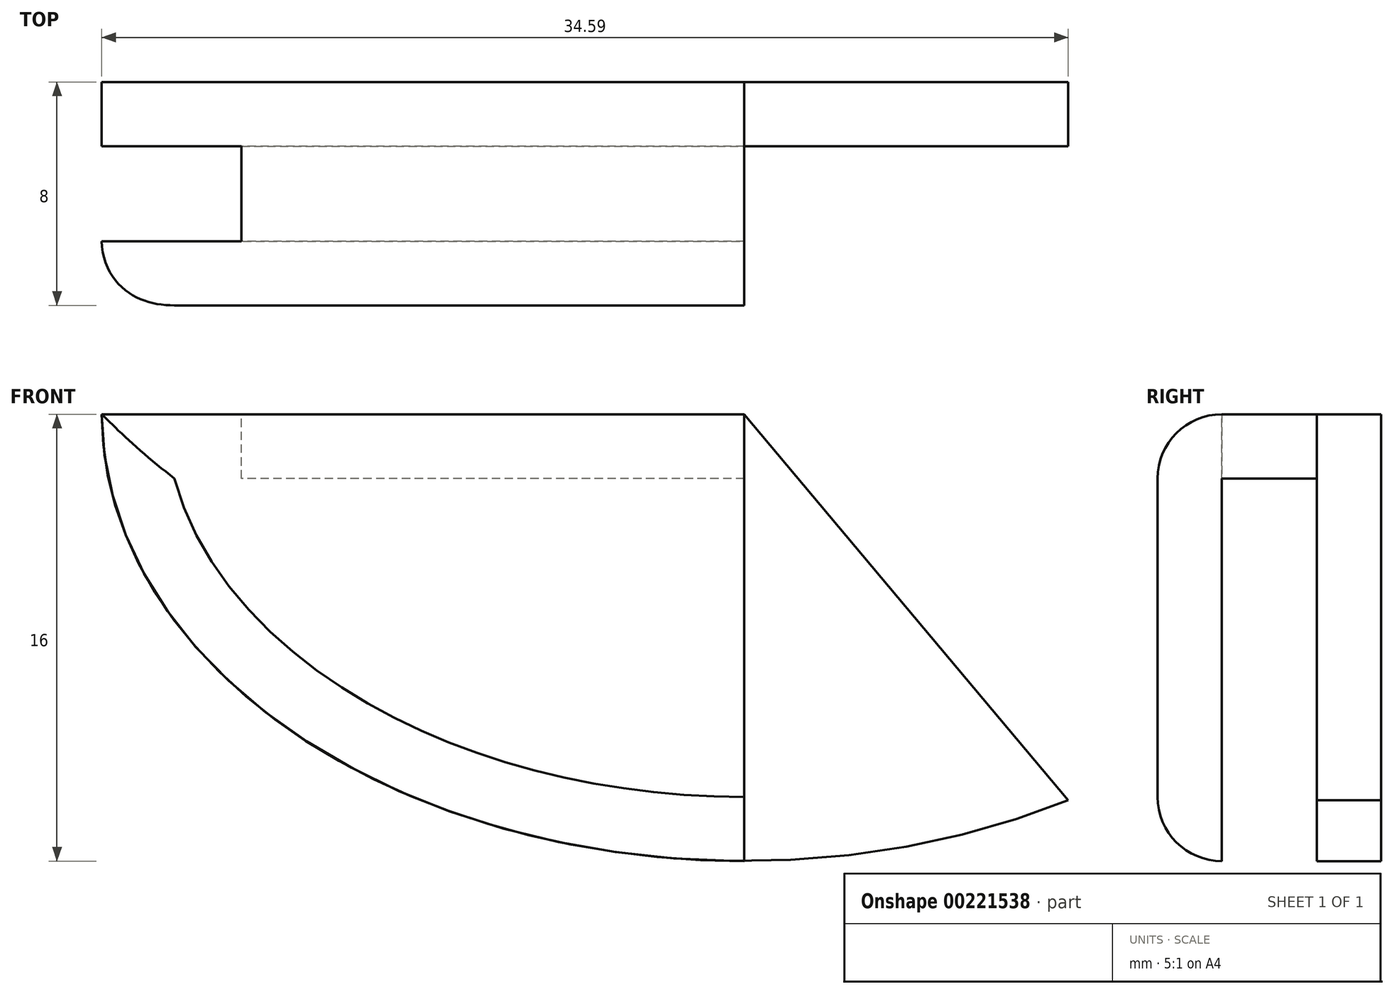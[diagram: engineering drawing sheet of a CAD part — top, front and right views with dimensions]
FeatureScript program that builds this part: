
annotation { "Feature Type Name" : "Feature", "Feature Type Description" : "" }
export const myFeature = defineFeature(function(context is Context, id is Id, definition is map)
    precondition{}
    {
        {
            var Q0;
            Q0=qCreatedBy(makeId("Front.planeOp"),FACE);
            var sketch = newSketch(context, id + "F0", { "sketchPlane" : qUnion([Q0])});
            skEllipse(sketch, "E0", {"center": v(0, 0) * mm, "majorRadius": 23 * mm, "minorRadius": 16 * mm, "majorAxis": v(-1, 0)});
            skLineSegment(sketch, "E1", {"start": v(-23, 0) * mm, "end": v(0, 0) * mm});
            skLineSegment(sketch, "E2", {"start": v(0, -16) * mm, "end": v(0, 0) * mm});
            skLineSegment(sketch, "E3", {"start": v(0, -2.3) * mm, "end": v(-22.76, -2.3) * mm});
            skLineSegment(sketch, "E4", {"start": v(0, 0) * mm, "end": v(11.6, -13.82) * mm});
            skLineSegment(sketch, "E5", {"start": v(-18, -2.3) * mm, "end": v(-18, 0) * mm});
            skSolve(sketch);
        }
        {
            var Q0;
            {var subQ5=sQuery(id+"F0.wireOp",EDGE,"E5");Q0=makeQuery(id+"F0.imprint","IMPRINT",FACE,{"disambiguationData":[TD([[makeQuery(id+"F0.imprint","IMPRINT",EDGE,{"derivedFrom":subQ5}),1.0]])]});}
            var Q1;
            {var subQ3=sQuery(id+"F0.wireOp",EDGE,"E5");Q1=makeQuery(id+"F0.imprint","IMPRINT",FACE,{"disambiguationData":[TD([[makeQuery(id+"F0.imprint","IMPRINT",EDGE,{"derivedFrom":subQ3}),-1.0]])]});}
            var Q2;
            {var subQ0=sQuery(id+"F0.wireOp",EDGE,"E2");var subQ1=sQuery(id+"F0.wireOp",EDGE,"E0");var subQ2=makeQuery(id+"F0.imprint","INTERSECT",VERTEX,{"derivedFrom":[subQ1,subQ0]});Q2=makeQuery(id+"F0.imprint","IMPRINT",FACE,{"disambiguationData":[TD([[makeQuery(id+"F0.imprint","IMPRINT",EDGE,{"disambiguationData":[TD([[subQ2,1.0]])],"derivedFrom":subQ1}),1.0]])]});}
            var Q3;
            {var subQ3=sQuery(id+"F0.wireOp",EDGE,"E4");Q3=makeQuery(id+"F0.imprint","IMPRINT",FACE,{"disambiguationData":[TD([[makeQuery(id+"F0.imprint","IMPRINT",EDGE,{"derivedFrom":subQ3}),-1.0]])]});}
            extrude(context, id + "F1", {"entities" : qUnion([Q0, Q1, Q2, Q3]), "oppositeDirection" : true, "depth" : 4 * mm});
        }
        {
            var Q0;
            {var subQ3=sQuery(id+"F0.wireOp",EDGE,"E5");Q0=makeQuery(id+"F0.imprint","IMPRINT",FACE,{"disambiguationData":[TD([[makeQuery(id+"F0.imprint","IMPRINT",EDGE,{"derivedFrom":subQ3}),-1.0]])]});}
            var Q1;
            {var subQ5=sQuery(id+"F0.wireOp",EDGE,"E5");Q1=makeQuery(id+"F0.imprint","IMPRINT",FACE,{"disambiguationData":[TD([[makeQuery(id+"F0.imprint","IMPRINT",EDGE,{"derivedFrom":subQ5}),1.0]])]});}
            var Q2;
            {var subQ0=sQuery(id+"F0.wireOp",EDGE,"E2");var subQ1=sQuery(id+"F0.wireOp",EDGE,"E0");var subQ2=makeQuery(id+"F0.imprint","INTERSECT",VERTEX,{"derivedFrom":[subQ1,subQ0]});Q2=makeQuery(id+"F0.imprint","IMPRINT",FACE,{"disambiguationData":[TD([[makeQuery(id+"F0.imprint","IMPRINT",EDGE,{"disambiguationData":[TD([[subQ2,1.0]])],"derivedFrom":subQ1}),1.0]])]});}
            extrude(context, id + "F2", {"entities" : qUnion([Q0, Q1, Q2]), "operationType" : NewBodyOperationType.ADD, "depth" : 4 * mm});
        }
        {
            var Q0;
            {var subQ5=sQuery(id+"F0.wireOp",EDGE,"E5");Q0=makeQuery(id+"F0.imprint","IMPRINT",FACE,{"disambiguationData":[TD([[makeQuery(id+"F0.imprint","IMPRINT",EDGE,{"derivedFrom":subQ5}),1.0]])]});}
            var Q1;
            {var subQ0=sQuery(id+"F0.wireOp",EDGE,"E2");var subQ1=sQuery(id+"F0.wireOp",EDGE,"E0");var subQ2=makeQuery(id+"F0.imprint","INTERSECT",VERTEX,{"derivedFrom":[subQ1,subQ0]});Q1=makeQuery(id+"F0.imprint","IMPRINT",FACE,{"disambiguationData":[TD([[makeQuery(id+"F0.imprint","IMPRINT",EDGE,{"disambiguationData":[TD([[subQ2,1.0]])],"derivedFrom":subQ1}),1.0]])]});}
            var Q2;
            {var subQ3=sQuery(id+"F0.wireOp",EDGE,"E4");Q2=makeQuery(id+"F0.imprint","IMPRINT",FACE,{"disambiguationData":[TD([[makeQuery(id+"F0.imprint","IMPRINT",EDGE,{"derivedFrom":subQ3}),-1.0]])]});}
            extrude(context, id + "F3", {"entities" : qUnion([Q0, Q1, Q2]), "operationType" : NewBodyOperationType.REMOVE, "endBound" : BoundingType.SYMMETRIC, "oppositeDirection" : true, "depth" : 3.4 * mm});
        }
        {
            var Q0;
            Q0=makeQuery(id+"F2.opExtrude","CAP_EDGE",EDGE,{"disambiguationData":[OSD([sQuery(id+"F0.wireOp",EDGE,"E1")])],"isStart":false});
            var Q1;
            Q1=makeQuery(id+"F2.opExtrude","CAP_EDGE",EDGE,{"disambiguationData":[OSD([sQuery(id+"F0.wireOp",EDGE,"E0")])],"isStart":false});
            fillet(context, id + "F4", {"entities" : qUnion([Q0, Q1]), "radius" : 2.3 * mm, "tangentPropagation" : true, "allowEdgeOverflow" : false});
        }
    });
